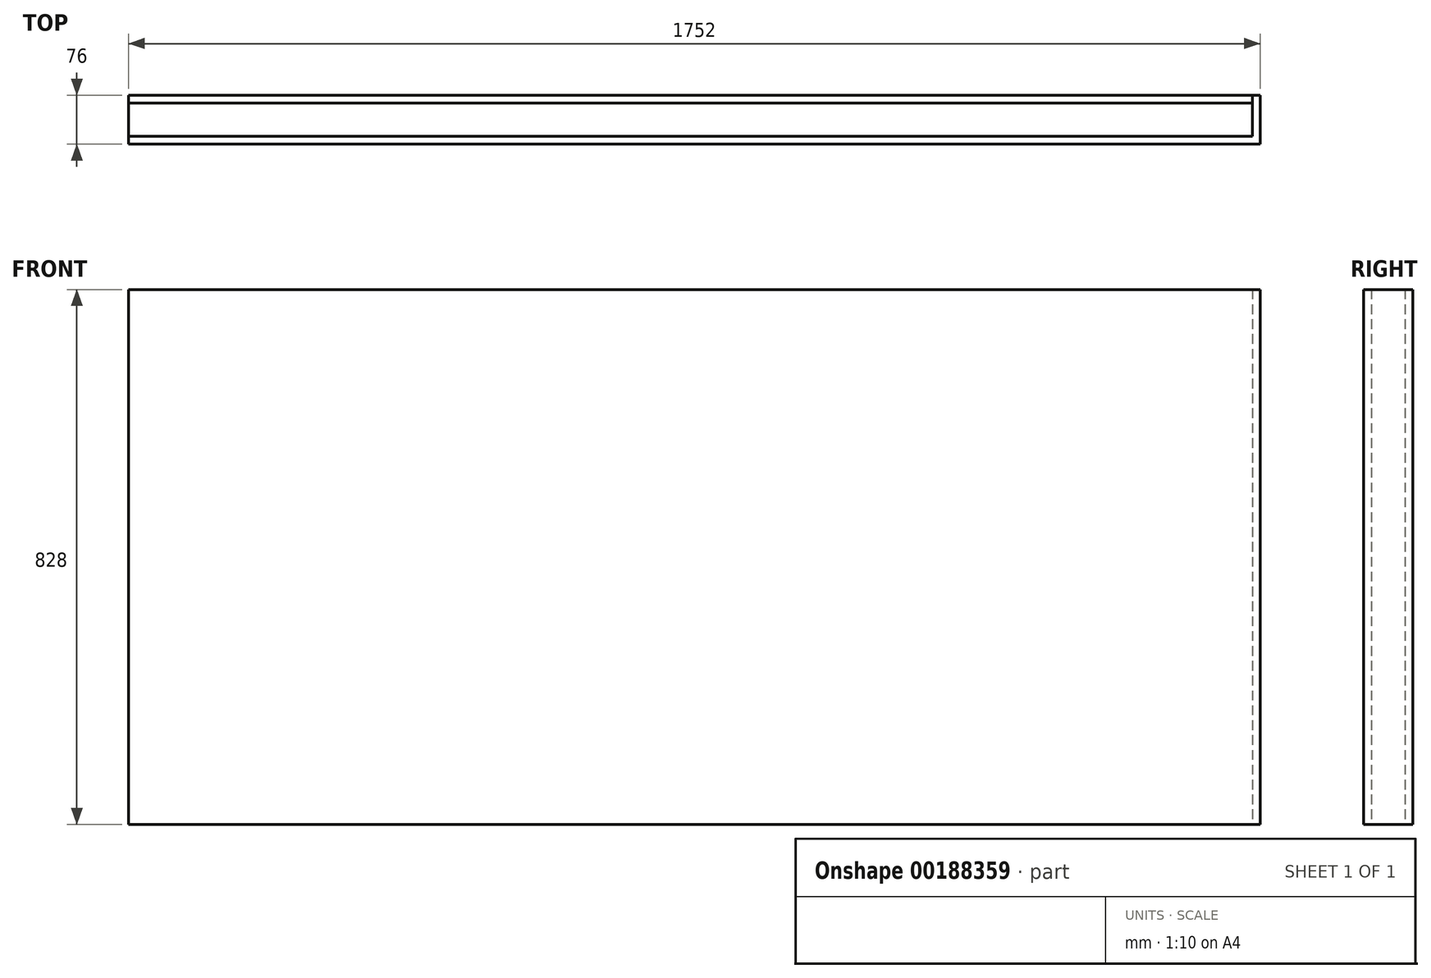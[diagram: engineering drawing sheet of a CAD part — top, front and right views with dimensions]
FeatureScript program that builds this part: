
annotation { "Feature Type Name" : "Feature", "Feature Type Description" : "" }
export const myFeature = defineFeature(function(context is Context, id is Id, definition is map)
    precondition{}
    {
        {
            var Q0;
            Q0=qCreatedBy(makeId("Top.planeOp"),FACE);
            var sketch = newSketch(context, id + "F0", { "sketchPlane" : qUnion([Q0])});
            skLineSegment(sketch, "E0.bottom", {"start": v(870, -26) * mm, "end": v(-870, -26) * mm});
            skLineSegment(sketch, "E0.top", {"start": v(870, 26) * mm, "end": v(-870, 26) * mm});
            skLineSegment(sketch, "E0.left", {"start": v(870, -26) * mm, "end": v(870, 26) * mm});
            skLineSegment(sketch, "E0.right", {"start": v(-870, -26) * mm, "end": v(-870, 26) * mm});
            skPoint(sketch, "E0.middle", {"position": v(0, 0) * mm});
            skSolve(sketch);
        }
        {
            var Q0;
            Q0=makeQuery(id+"F0.imprint","IMPRINT",FACE,{"disambiguationData":[TD([[makeQuery(id+"F0.imprint","IMPRINT",EDGE,{"derivedFrom":sQuery(id+"F0.wireOp",EDGE,"E0.bottom")}),-1.0]])]});
            extrude(context, id + "F1", {"entities" : qUnion([Q0]), "depth" : 828 * mm});
        }
        {
            var Q0;
            Q0=qCreatedBy(makeId("Top.planeOp"),FACE);
            var sketch = newSketch(context, id + "F2", { "sketchPlane" : qUnion([Q0])});
            skLineSegment(sketch, "E1", {"start": v(-870, -26) * mm, "end": v(870, -26) * mm});
            skLineSegment(sketch, "E2", {"start": v(870, -26) * mm, "end": v(870, 38) * mm});
            skLineSegment(sketch, "E3", {"start": v(870, 38) * mm, "end": v(882, 38) * mm});
            skLineSegment(sketch, "E4", {"start": v(882, 38) * mm, "end": v(882, -38) * mm});
            skLineSegment(sketch, "E5", {"start": v(882, -38) * mm, "end": v(-870, -38) * mm});
            skLineSegment(sketch, "E6", {"start": v(-870, -38) * mm, "end": v(-870, -26) * mm});
            skSolve(sketch);
        }
        {
            var Q0;
            Q0=makeQuery(id+"F2.imprint","IMPRINT",FACE,{"disambiguationData":[TD([[makeQuery(id+"F2.imprint","IMPRINT",EDGE,{"derivedFrom":sQuery(id+"F2.wireOp",EDGE,"E1")}),-1.0]])]});
            var Q1;
            Q1=makeQuery(id+"F1.opExtrude","CAP_VERTEX",VERTEX,{"disambiguationData":[OSD([sQuery(id+"F0.wireOp",EDGE,"E0.bottom"),sQuery(id+"F0.wireOp",EDGE,"E0.left")])],"isStart":false});
            extrude(context, id + "F3", {"entities" : qUnion([Q0]), "endBound" : BoundingType.UP_TO_VERTEX, "endBoundEntityVertex" : qUnion([Q1]), "depth" : 25 * mm});
        }
        {
            var Q0;
            Q0=qCreatedBy(makeId("Top.planeOp"),FACE);
            var sketch = newSketch(context, id + "F4", { "sketchPlane" : qUnion([Q0])});
            skLineSegment(sketch, "E7.bottom", {"start": v(-870, 26) * mm, "end": v(870, 26) * mm});
            skLineSegment(sketch, "E7.top", {"start": v(-870, 38) * mm, "end": v(870, 38) * mm});
            skLineSegment(sketch, "E7.left", {"start": v(-870, 26) * mm, "end": v(-870, 38) * mm});
            skLineSegment(sketch, "E7.right", {"start": v(870, 26) * mm, "end": v(870, 38) * mm});
            skSolve(sketch);
        }
        {
            var Q0;
            Q0 = qSketchRegion(id + "F4", true);
            var Q1;
            Q1=makeQuery(id+"F1.opExtrude","CAP_VERTEX",VERTEX,{"disambiguationData":[OSD([sQuery(id+"F0.wireOp",EDGE,"E0.top"),sQuery(id+"F0.wireOp",EDGE,"E0.right")])],"isStart":false});
            extrude(context, id + "F5", {"entities" : qUnion([Q0]), "endBound" : BoundingType.UP_TO_VERTEX, "endBoundEntityVertex" : qUnion([Q1]), "depth" : 25 * mm});
        }
    });
